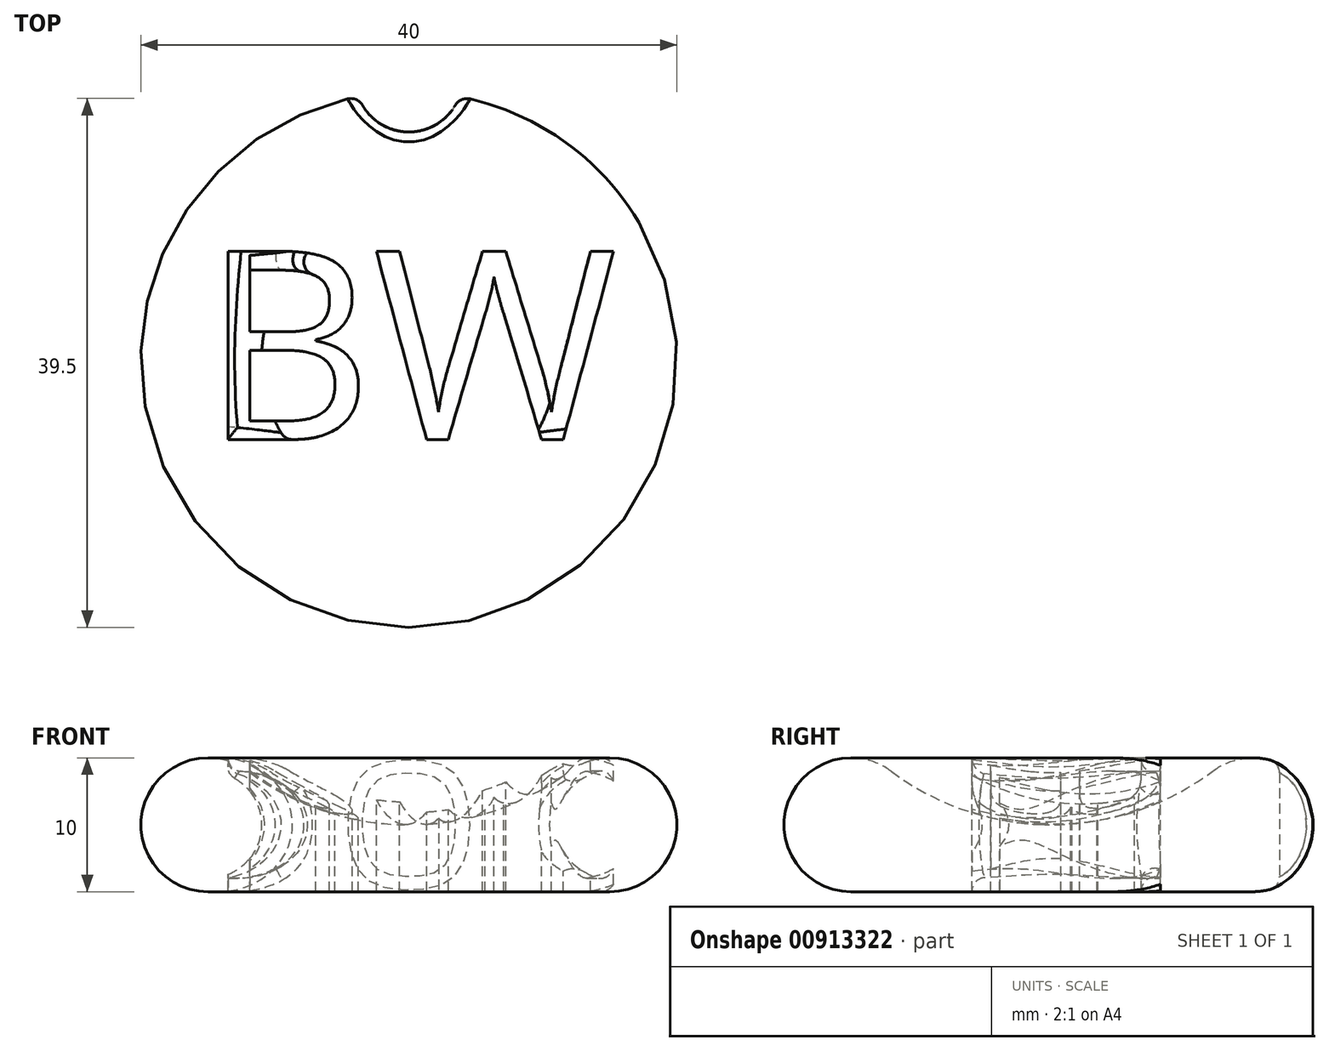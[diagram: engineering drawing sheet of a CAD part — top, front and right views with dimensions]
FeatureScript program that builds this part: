
annotation { "Feature Type Name" : "Feature", "Feature Type Description" : "" }
export const myFeature = defineFeature(function(context is Context, id is Id, definition is map)
    precondition{}
    {
        {
            var Q0;
            Q0=qCreatedBy(makeId("Front.planeOp"),FACE);
            var sketch = newSketch(context, id + "F0", { "sketchPlane" : qUnion([Q0])});
            skArc(sketch, "E0", {"start": v(-12, 9) * mm, "mid": v(-19.74, 6.58) * mm, "end": v(-15, 0) * mm});
            skArc(sketch, "E1", {"start": v(-12, 9) * mm, "mid": v(-6.32, 6.03) * mm, "end": v(0, 5) * mm});
            skLineSegment(sketch, "E2", {"start": v(0, 0) * mm, "end": v(-15, 0) * mm});
            skLineSegment(sketch, "E3", {"start": v(0, 0) * mm, "end": v(0, 5) * mm});
            skSolve(sketch);
        }
        {
            var Q0;
            Q0=makeQuery(id+"F0.imprint","IMPRINT",FACE,{"disambiguationData":[TD([[makeQuery(id+"F0.imprint","IMPRINT",EDGE,{"derivedFrom":sQuery(id+"F0.wireOp",EDGE,"E0")}),1.0]])]});
            var Q1;
            Q1=sQuery(id+"F0.wireOp",EDGE,"E3");
            revolve(context, id + "F1", {"surfaceOperationType" : NewSurfaceOperationType.NEW, "entities" : qUnion([Q0]), "axis" : qUnion([Q1]), "revolveType" : RevolveType.FULL});
        }
        {
            var Q0;
            Q0=qCreatedBy(makeId("Top.planeOp"),FACE);
            cPlane(context, id + "F2", {"entities" : qUnion([Q0]), "cplaneType" : CPlaneType.OFFSET, "offset" : 10 * mm, "width" : 150 * mm, "height" : 150 * mm});
        }
        {
            var Q0;
            Q0=qCreatedBy(id+"F2.planeOp",FACE);
            var sketch = newSketch(context, id + "F3", { "sketchPlane" : qUnion([Q0])});
            skText(sketch, "E4", { "text": "BW", "fontName": "OpenSans-Regular.ttf"});
            const initialGuessF3  = {"E4": [-0.01544, -0.00597, 1, 0, 0.01418]};
            skSetInitialGuess(sketch, initialGuessF3);
            skSolve(sketch);
        }
        {
            var Q0;
            Q0=qSketchRegion(id+"F3",true);
            extrude(context, id + "F4", {"entities" : qUnion([Q0]), "operationType" : NewBodyOperationType.REMOVE, "oppositeDirection" : true, "depth" : 25 * mm, "offsetDistance" : 25 * mm});
        }
        {
            var Q0;
            Q0=qCreatedBy(makeId("Front.planeOp"),FACE);
            var sketch = newSketch(context, id + "F5", { "sketchPlane" : qUnion([Q0])});
            skCircle(sketch, "E5", {"center": v(-15, 5) * mm, "radius": 4 * mm});
            skSolve(sketch);
        }
        {
            var Q0;
            Q0=qSketchRegion(id+"F5",true);
            var Q1;
            Q1=sQuery(id+"F0.wireOp",EDGE,"E3");
            revolve(context, id + "F6", {"operationType" : NewBodyOperationType.ADD, "surfaceOperationType" : NewSurfaceOperationType.NEW, "entities" : qUnion([Q0]), "axis" : qUnion([Q1]), "revolveType" : RevolveType.FULL});
        }
        {
            var Q0;
            Q0=qCreatedBy(makeId("Top.planeOp"),FACE);
            var sketch = newSketch(context, id + "F7", { "sketchPlane" : qUnion([Q0])});
            skCircle(sketch, "E6", {"center": v(0, 21) * mm, "radius": 4 * mm});
            skSolve(sketch);
        }
        {
            var Q0;
            Q0=qSketchRegion(id+"F7",true);
            extrude(context, id + "F8", {"entities" : qUnion([Q0]), "operationType" : NewBodyOperationType.REMOVE, "depth" : 25 * mm, "offsetDistance" : 25 * mm});
        }
        {
            var Q0;
            Q0=makeQuery(id+"F8.boolean.opBoolean","INTERSECT",EDGE,{"derivedFrom":[makeQuery(id+"F4.boolean.opBoolean","SPLIT",FACE,{"disambiguationData":[TD([makeQuery(id+"F1.opRevolve","SWEPT_FACE",FACE,{"disambiguationData":[OSD([sQuery(id+"F0.wireOp",EDGE,"E2")])]})])],"derivedFrom":makeQuery(id+"F1.opRevolve","SWEPT_FACE",FACE,{"disambiguationData":[OSD([sQuery(id+"F0.wireOp",EDGE,"E0")])]})}),makeQuery(id+"F8.opExtrude","SWEPT_FACE",FACE,{"disambiguationData":[OSD([sQuery(id+"F7.wireOp",EDGE,"E6")])]})]});
            fillet(context, id + "F9", {"entities" : qUnion([Q0]), "radius" : 1 * mm, "tangentPropagation" : true, "allowEdgeOverflow" : false});
        }
        {
            var Q0;
            Q0=makeQuery(id+"F6.boolean.opBoolean","INTERSECT",EDGE,{"disambiguationData":[OD(0.0)],"derivedFrom":[makeQuery(id+"F4.boolean.opBoolean","COPY",FACE,{"derivedFrom":makeQuery(id+"F4.opExtrude","SWEPT_FACE",FACE,{"disambiguationData":[OSD([sQuery(id+"F3.wireOp",EDGE,"E4.sketch_text.stroke-16")])]})}),makeQuery(id+"F6.opRevolve","SWEPT_FACE",FACE,{"disambiguationData":[OSD([sQuery(id+"F5.wireOp",EDGE,"E5")])]})]});
            var Q1;
            Q1=makeQuery(id+"F6.boolean.opBoolean","INTERSECT",EDGE,{"disambiguationData":[OD(0.0)],"derivedFrom":[makeQuery(id+"F4.boolean.opBoolean","COPY",FACE,{"derivedFrom":makeQuery(id+"F4.opExtrude","SWEPT_FACE",FACE,{"disambiguationData":[OSD([sQuery(id+"F3.wireOp",EDGE,"E4.sketch_text.stroke-25")])]})}),makeQuery(id+"F6.opRevolve","SWEPT_FACE",FACE,{"disambiguationData":[OSD([sQuery(id+"F5.wireOp",EDGE,"E5")])]})]});
            var Q2;
            Q2=makeQuery(id+"F6.boolean.opBoolean","INTERSECT",EDGE,{"disambiguationData":[OD(1.0)],"derivedFrom":[makeQuery(id+"F4.boolean.opBoolean","COPY",FACE,{"derivedFrom":makeQuery(id+"F4.opExtrude","SWEPT_FACE",FACE,{"disambiguationData":[OSD([sQuery(id+"F3.wireOp",EDGE,"E4.sketch_text.stroke-10")])]})}),makeQuery(id+"F6.opRevolve","SWEPT_FACE",FACE,{"disambiguationData":[OSD([sQuery(id+"F5.wireOp",EDGE,"E5")])]})]});
            var Q3;
            Q3=makeQuery(id+"F6.boolean.opBoolean","INTERSECT",EDGE,{"disambiguationData":[OD(1.0)],"derivedFrom":[makeQuery(id+"F4.boolean.opBoolean","COPY",FACE,{"derivedFrom":makeQuery(id+"F4.opExtrude","SWEPT_FACE",FACE,{"disambiguationData":[OSD([sQuery(id+"F3.wireOp",EDGE,"E4.sketch_text.stroke-9")])]})}),makeQuery(id+"F6.opRevolve","SWEPT_FACE",FACE,{"disambiguationData":[OSD([sQuery(id+"F5.wireOp",EDGE,"E5")])]})]});
            var Q4;
            Q4=makeQuery(id+"F6.boolean.opBoolean","INTERSECT",EDGE,{"disambiguationData":[OD(1.0)],"derivedFrom":[makeQuery(id+"F4.boolean.opBoolean","COPY",FACE,{"derivedFrom":makeQuery(id+"F4.opExtrude","SWEPT_FACE",FACE,{"disambiguationData":[OSD([sQuery(id+"F3.wireOp",EDGE,"E4.sketch_text.stroke-8")])]})}),makeQuery(id+"F6.opRevolve","SWEPT_FACE",FACE,{"disambiguationData":[OSD([sQuery(id+"F5.wireOp",EDGE,"E5")])]})]});
            fillet(context, id + "F10", {"entities" : qUnion([Q0, Q1, Q2, Q3, Q4]), "radius" : 1 * mm, "tangentPropagation" : true, "allowEdgeOverflow" : false});
        }
    });
